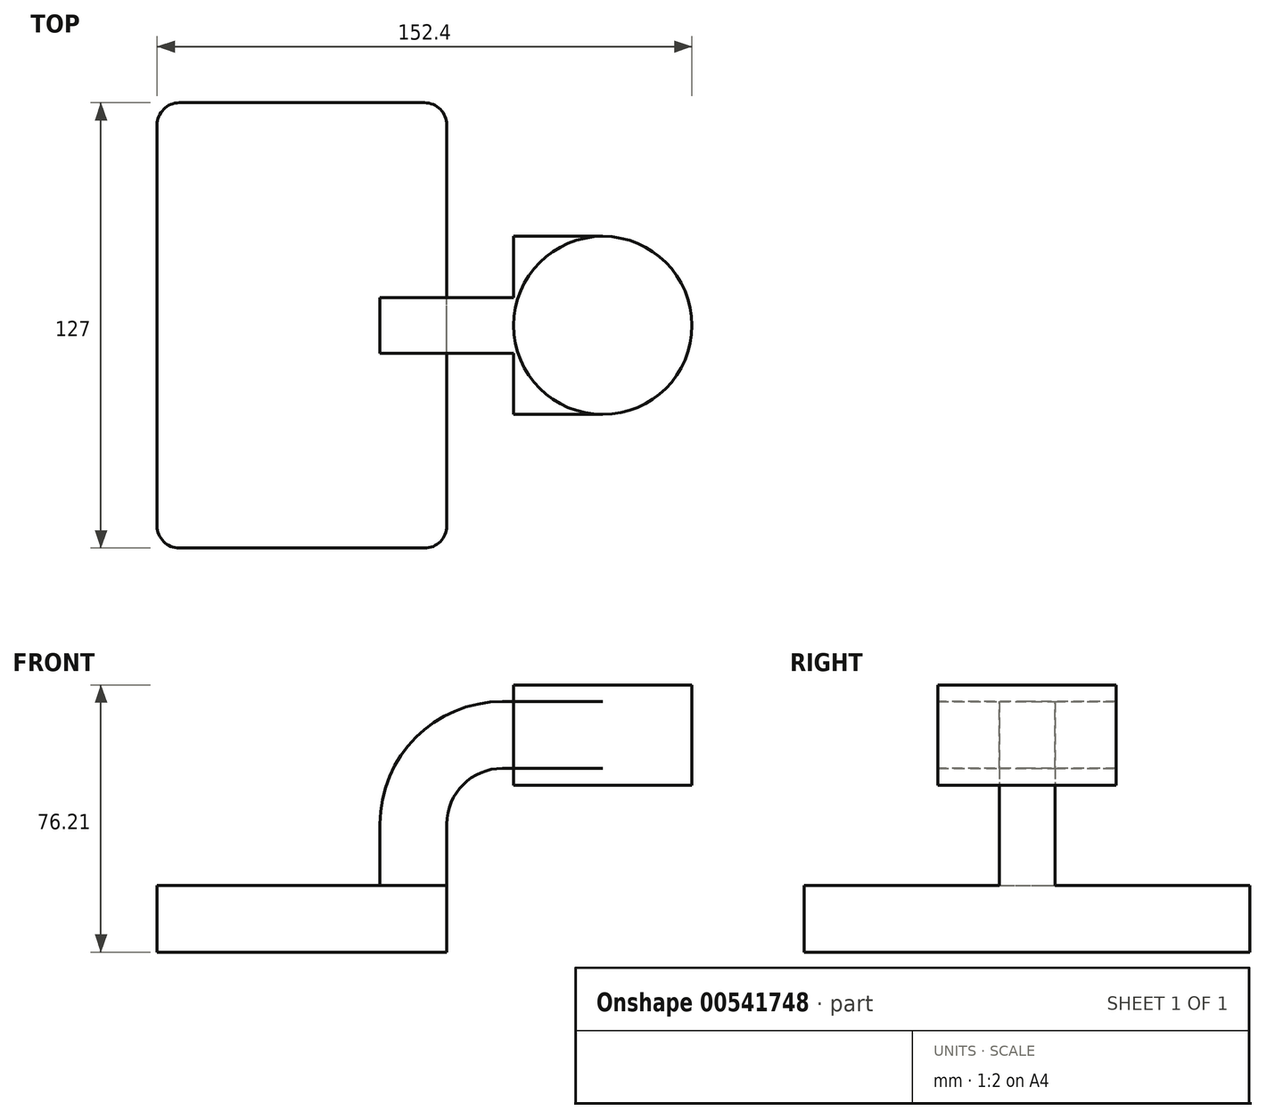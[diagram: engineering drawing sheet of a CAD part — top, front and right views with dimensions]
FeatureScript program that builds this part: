
annotation { "Feature Type Name" : "Feature", "Feature Type Description" : "" }
export const myFeature = defineFeature(function(context is Context, id is Id, definition is map)
    precondition{}
    {
        {
            var Q0;
            Q0=qCreatedBy(makeId("Front.planeOp"),FACE);
            var sketch = newSketch(context, id + "F0", { "sketchPlane" : qUnion([Q0])});
            skLineSegment(sketch, "E0.bottom", {"start": v(-41.27, -9.53) * mm, "end": v(41.28, -9.53) * mm});
            skLineSegment(sketch, "E0.top", {"start": v(-41.28, 9.53) * mm, "end": v(41.28, 9.53) * mm});
            skLineSegment(sketch, "E0.left", {"start": v(-41.28, -9.53) * mm, "end": v(-41.28, 9.53) * mm});
            skLineSegment(sketch, "E0.right", {"start": v(41.28, -9.53) * mm, "end": v(41.28, 9.53) * mm});
            skPoint(sketch, "E0.middle", {"position": v(0, 0) * mm});
            skLineSegment(sketch, "E1.bottom", {"start": v(60.32, 38.1) * mm, "end": v(111.12, 38.1) * mm});
            skLineSegment(sketch, "E1.top", {"start": v(60.32, 66.67) * mm, "end": v(111.12, 66.67) * mm});
            skLineSegment(sketch, "E1.left", {"start": v(60.32, 38.1) * mm, "end": v(60.32, 66.67) * mm});
            skLineSegment(sketch, "E1.right", {"start": v(111.12, 38.1) * mm, "end": v(111.12, 66.68) * mm});
            skPoint(sketch, "E1.middle", {"position": v(85.72, 52.39) * mm});
            skLineSegment(sketch, "E2", {"start": v(41.28, 9.53) * mm, "end": v(41.28, 27) * mm});
            skArc(sketch, "E3", {"start": v(41.27, 27) * mm, "mid": v(45.92, 38.23) * mm, "end": v(57.15, 42.88) * mm});
            skLineSegment(sketch, "E4", {"start": v(57.15, 42.88) * mm, "end": v(85.72, 42.88) * mm});
            skLineSegment(sketch, "E5.2", {"start": v(41.27, 9.53) * mm, "end": v(41.27, 27) * mm});
            skLineSegment(sketch, "E6.0", {"start": v(57.15, 61.93) * mm, "end": v(85.72, 61.93) * mm});
            skArc(sketch, "E6.1", {"start": v(22.22, 27) * mm, "mid": v(32.45, 51.7) * mm, "end": v(57.15, 61.93) * mm});
            skLineSegment(sketch, "E6.2", {"start": v(22.22, 9.53) * mm, "end": v(22.22, 27) * mm});
            skLineSegment(sketch, "E7", {"start": v(85.72, 38.1) * mm, "end": v(85.72, 66.68) * mm});
            skFitSpline(sketch, "E8", {"points": [v(-41.27, 9.53) * mm, v(57.15, 61.93) * mm], "startDerivative": vector(39.3, 109.13) * mm, "endDerivative": vector(141.93, -0.04) * mm});
            skSolve(sketch);
        }
        {
            var Q0;
            Q0=makeQuery(id+"F0.imprint","IMPRINT",FACE,{"disambiguationData":[TD([[makeQuery(id+"F0.imprint","IMPRINT",EDGE,{"derivedFrom":sQuery(id+"F0.wireOp",EDGE,"E0.bottom")}),1.0]])]});
            extrude(context, id + "F1", {"entities" : qUnion([Q0]), "endBound" : BoundingType.SYMMETRIC, "depth" : 127 * mm, "offsetDistance" : 25.4 * mm});
        }
        {
            var Q0;
            {var subQ0=sQuery(id+"F0.wireOp",EDGE,"E3");Q0=makeQuery(id+"F0.imprint","IMPRINT",FACE,{"disambiguationData":[TD([[makeQuery(id+"F0.imprint","IMPRINT",EDGE,{"derivedFrom":subQ0}),1.0]])]});}
            var Q1;
            {var subQ0=sQuery(id+"F0.wireOp",EDGE,"E4");var subQ1=sQuery(id+"F0.wireOp",EDGE,"E1.left");var subQ2=makeQuery(id+"F0.imprint","INTERSECT",VERTEX,{"derivedFrom":[subQ1,subQ0]});Q1=makeQuery(id+"F0.imprint","IMPRINT",FACE,{"disambiguationData":[TD([[makeQuery(id+"F0.imprint","IMPRINT",EDGE,{"disambiguationData":[TD([[subQ2,-1.0]])],"derivedFrom":subQ1}),-1.0]])]});}
            extrude(context, id + "F2", {"entities" : qUnion([Q0, Q1]), "operationType" : NewBodyOperationType.ADD, "endBound" : BoundingType.SYMMETRIC, "depth" : 50.8 * mm, "offsetDistance" : 25.4 * mm});
        }
        {
            var Q0;
            Q0=makeQuery(id+"F0.imprint","IMPRINT",FACE,{"disambiguationData":[TD([[makeQuery(id+"F0.imprint","IMPRINT",EDGE,{"derivedFrom":sQuery(id+"F0.wireOp",EDGE,"E6.1")}),1.0]])]});
            extrude(context, id + "F3", {"entities" : qUnion([Q0]), "operationType" : NewBodyOperationType.ADD, "endBound" : BoundingType.SYMMETRIC, "depth" : 15.88 * mm, "offsetDistance" : 25.4 * mm});
        }
        {
            var Q0;
            {var subQ0=sQuery(id+"F0.wireOp",EDGE,"E1.right");Q0=makeQuery(id+"F0.imprint","IMPRINT",FACE,{"disambiguationData":[TD([[makeQuery(id+"F0.imprint","IMPRINT",EDGE,{"derivedFrom":subQ0}),1.0]])]});}
            var Q1;
            Q1=sQuery(id+"F0.wireOp",EDGE,"E7");
            revolve(context, id + "F4", {"operationType" : NewBodyOperationType.ADD, "entities" : qUnion([Q0]), "axis" : qUnion([Q1]), "revolveType" : RevolveType.FULL});
        }
        {
            var Q0;
            Q0=makeQuery(id+"F1.opExtrude","CAP_EDGE",EDGE,{"disambiguationData":[OSD([sQuery(id+"F0.wireOp",EDGE,"E0.left")])],"isStart":false});
            var Q1;
            Q1=makeQuery(id+"F1.opExtrude","CAP_EDGE",EDGE,{"disambiguationData":[OSD([sQuery(id+"F0.wireOp",EDGE,"E0.right")])],"isStart":false});
            var Q2;
            Q2=makeQuery(id+"F1.opExtrude","CAP_EDGE",EDGE,{"disambiguationData":[OSD([sQuery(id+"F0.wireOp",EDGE,"E0.right")])],"isStart":true});
            var Q3;
            Q3=makeQuery(id+"F1.opExtrude","CAP_EDGE",EDGE,{"disambiguationData":[OSD([sQuery(id+"F0.wireOp",EDGE,"E0.left")])],"isStart":true});
            fillet(context, id + "F5", {"entities" : qUnion([Q0, Q1, Q2, Q3]), "radius" : 6.35 * mm, "tangentPropagation" : true, "allowEdgeOverflow" : false});
        }
    });
